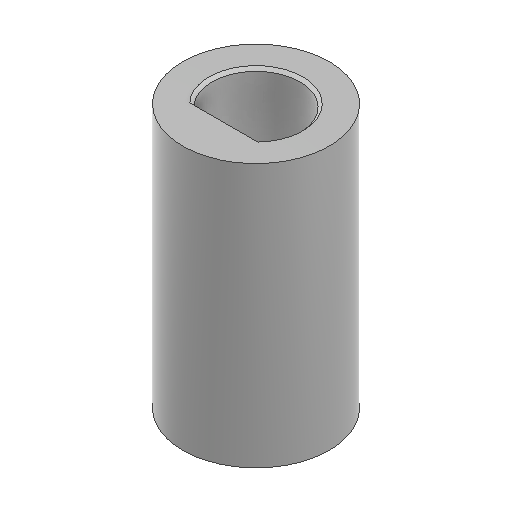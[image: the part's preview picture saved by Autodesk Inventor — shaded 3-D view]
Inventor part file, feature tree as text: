
AUTODESK INVENTOR PART (.ipt)
format: ipt  version: 2022 (Build 260153000, 153)  size: 124,416 bytes
history: native  units: mm
features: extrude x1, chamfer x1, sketch x1
ambient origin geometry x8: Origin, YZ Plane, XZ Plane, XY Plane, X Axis, Y Axis, Z Axis, Center Point
bodies: Body1 (feature_tree)
feature tree (3):
  extrude  "Выдавливание4"  Depth=3.0mm
  chamfer  "Фаска1"  Distance=2.236mm
  sketch  "Эскиз1"
